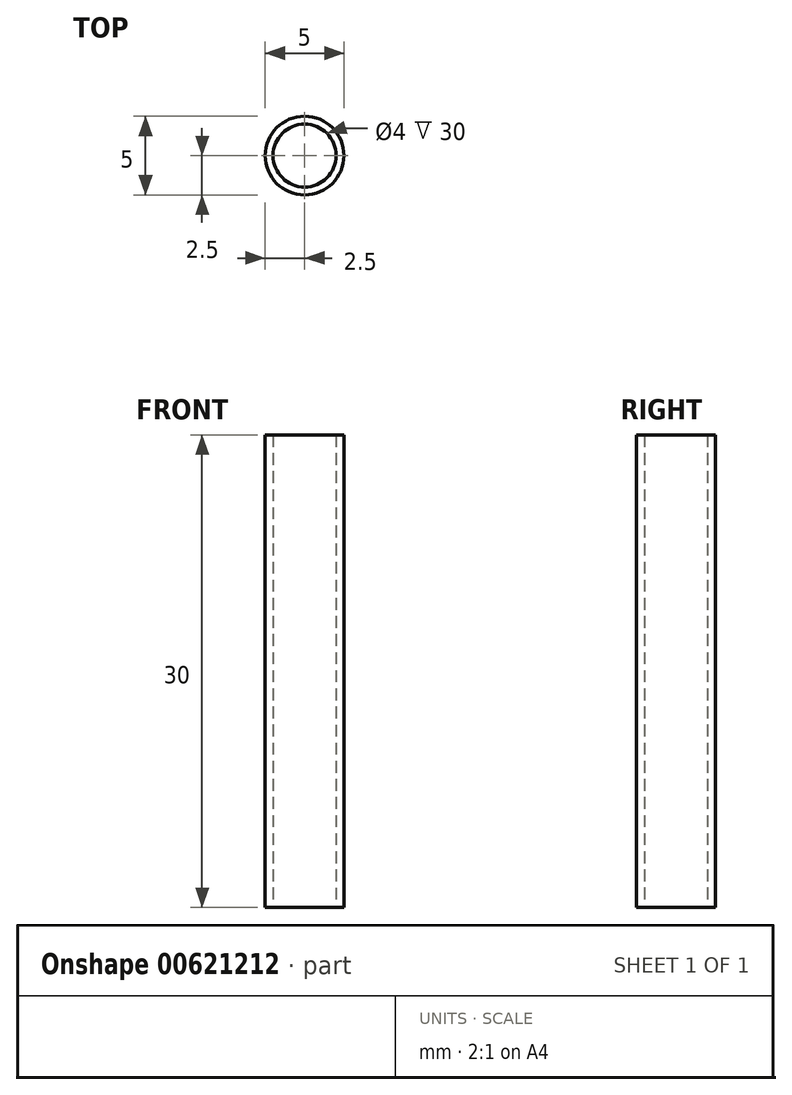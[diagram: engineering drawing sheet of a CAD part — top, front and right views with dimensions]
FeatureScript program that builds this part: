
annotation { "Feature Type Name" : "Feature", "Feature Type Description" : "" }
export const myFeature = defineFeature(function(context is Context, id is Id, definition is map)
    precondition{}
    {
        {
            var Q0;
            Q0=qCreatedBy(makeId("Top.planeOp"),FACE);
            var sketch = newSketch(context, id + "F0", { "sketchPlane" : qUnion([Q0])});
            skCircle(sketch, "E0", {"center": v(0, 0) * mm, "radius": 2.5 * mm});
            skCircle(sketch, "E1", {"center": v(0, 0) * mm, "radius": 2 * mm});
            skSolve(sketch);
        }
        {
            var Q0;
            Q0 = qSketchRegion(id + "F0", true);
            extrude(context, id + "F1", {"entities" : qUnion([Q0]), "depth" : 30 * mm, "offsetDistance" : 25 * mm});
        }
    });
